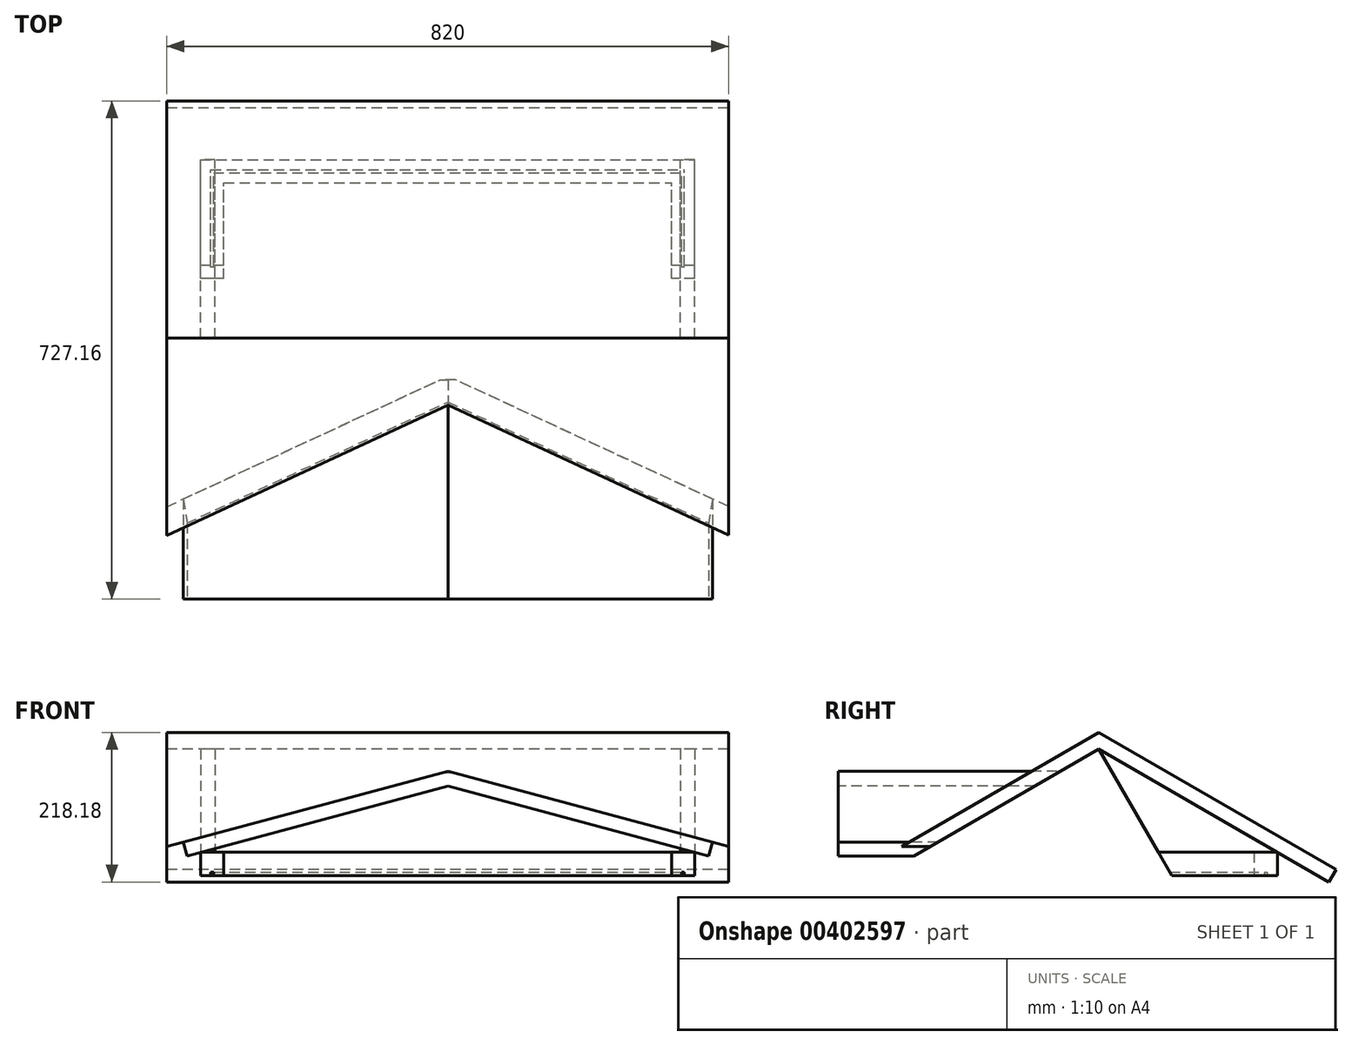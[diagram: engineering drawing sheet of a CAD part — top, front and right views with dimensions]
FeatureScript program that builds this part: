
annotation { "Feature Type Name" : "Feature", "Feature Type Description" : "" }
export const myFeature = defineFeature(function(context is Context, id is Id, definition is map)
    precondition{}
    {
        {
            var Q0;
            Q0=qCreatedBy(makeId("Top.planeOp"),FACE);
            var sketch = newSketch(context, id + "F0", { "sketchPlane" : qUnion([Q0])});
            skLineSegment(sketch, "E0.bottom", {"start": v(-361.13, -297.37) * mm, "end": v(360.37, -297.37) * mm});
            skLineSegment(sketch, "E0.top", {"start": v(-361.13, 224.13) * mm, "end": v(360.37, 224.13) * mm});
            skLineSegment(sketch, "E0.left", {"start": v(-361.13, -297.37) * mm, "end": v(-361.13, 224.13) * mm});
            skLineSegment(sketch, "E0.right", {"start": v(360.37, -297.37) * mm, "end": v(360.37, 224.13) * mm});
            skLineSegment(sketch, "E1.0", {"start": v(326.37, -263.37) * mm, "end": v(326.37, 190.13) * mm});
            skLineSegment(sketch, "E1.1", {"start": v(-327.13, -263.37) * mm, "end": v(326.37, -263.37) * mm});
            skLineSegment(sketch, "E1.2", {"start": v(-327.13, -263.37) * mm, "end": v(-327.13, 190.13) * mm});
            skLineSegment(sketch, "E1.3", {"start": v(-327.13, 190.13) * mm, "end": v(326.37, 190.13) * mm});
            skLineSegment(sketch, "E2.0", {"start": v(341.37, -278.37) * mm, "end": v(341.37, 205.13) * mm});
            skLineSegment(sketch, "E2.1", {"start": v(-342.13, -278.37) * mm, "end": v(341.37, -278.37) * mm});
            skLineSegment(sketch, "E2.2", {"start": v(-342.13, -278.37) * mm, "end": v(-342.13, 205.13) * mm});
            skLineSegment(sketch, "E2.3", {"start": v(-342.13, 205.13) * mm, "end": v(341.37, 205.13) * mm});
            skLineSegment(sketch, "E3.0", {"start": v(345.37, -282.37) * mm, "end": v(345.37, 209.13) * mm});
            skLineSegment(sketch, "E3.1", {"start": v(-346.13, -282.37) * mm, "end": v(345.37, -282.37) * mm});
            skLineSegment(sketch, "E3.2", {"start": v(-346.13, -282.37) * mm, "end": v(-346.13, 209.13) * mm});
            skLineSegment(sketch, "E3.3", {"start": v(-346.13, 209.13) * mm, "end": v(345.37, 209.13) * mm});
            skLineSegment(sketch, "E4", {"start": v(326.37, 190.13) * mm, "end": v(360.37, 224.13) * mm});
            skLineSegment(sketch, "E5", {"start": v(-327.13, 190.13) * mm, "end": v(-361.13, 224.13) * mm});
            skLineSegment(sketch, "E6", {"start": v(-327.13, -263.37) * mm, "end": v(-361.13, -297.37) * mm});
            skLineSegment(sketch, "E7", {"start": v(326.37, -263.37) * mm, "end": v(360.37, -297.37) * mm});
            skSolve(sketch);
        }
        {
            var Q0;
            {var subQ0=sQuery(id+"F0.wireOp",EDGE,"E0.right");Q0=makeQuery(id+"F0.imprint","IMPRINT",FACE,{"disambiguationData":[TD([[makeQuery(id+"F0.imprint","IMPRINT",EDGE,{"derivedFrom":subQ0}),1.0]])]});}
            var Q1;
            {var subQ0=sQuery(id+"F0.wireOp",EDGE,"E1.0");Q1=makeQuery(id+"F0.imprint","IMPRINT",FACE,{"disambiguationData":[TD([[makeQuery(id+"F0.imprint","IMPRINT",EDGE,{"derivedFrom":subQ0}),-1.0]])]});}
            var Q2;
            {var subQ0=sQuery(id+"F0.wireOp",EDGE,"E0.bottom");Q2=makeQuery(id+"F0.imprint","IMPRINT",FACE,{"disambiguationData":[TD([[makeQuery(id+"F0.imprint","IMPRINT",EDGE,{"derivedFrom":subQ0}),1.0]])]});}
            var Q3;
            {var subQ0=sQuery(id+"F0.wireOp",EDGE,"E0.top");Q3=makeQuery(id+"F0.imprint","IMPRINT",FACE,{"disambiguationData":[TD([[makeQuery(id+"F0.imprint","IMPRINT",EDGE,{"derivedFrom":subQ0}),-1.0]])]});}
            var Q4;
            {var subQ0=sQuery(id+"F0.wireOp",EDGE,"E0.left");Q4=makeQuery(id+"F0.imprint","IMPRINT",FACE,{"disambiguationData":[TD([[makeQuery(id+"F0.imprint","IMPRINT",EDGE,{"derivedFrom":subQ0}),-1.0]])]});}
            var Q5;
            {var subQ0=sQuery(id+"F0.wireOp",EDGE,"E1.1");Q5=makeQuery(id+"F0.imprint","IMPRINT",FACE,{"disambiguationData":[TD([[makeQuery(id+"F0.imprint","IMPRINT",EDGE,{"derivedFrom":subQ0}),-1.0]])]});}
            var Q6;
            {var subQ0=sQuery(id+"F0.wireOp",EDGE,"E1.2");Q6=makeQuery(id+"F0.imprint","IMPRINT",FACE,{"disambiguationData":[TD([[makeQuery(id+"F0.imprint","IMPRINT",EDGE,{"derivedFrom":subQ0}),1.0]])]});}
            var Q7;
            {var subQ0=sQuery(id+"F0.wireOp",EDGE,"E1.3");Q7=makeQuery(id+"F0.imprint","IMPRINT",FACE,{"disambiguationData":[TD([[makeQuery(id+"F0.imprint","IMPRINT",EDGE,{"derivedFrom":subQ0}),1.0]])]});}
            var Q8;
            {var subQ0=sQuery(id+"F0.wireOp",EDGE,"E2.0");Q8=makeQuery(id+"F0.imprint","IMPRINT",FACE,{"disambiguationData":[TD([[makeQuery(id+"F0.imprint","IMPRINT",EDGE,{"derivedFrom":subQ0}),-1.0]])]});}
            var Q9;
            {var subQ0=sQuery(id+"F0.wireOp",EDGE,"E2.1");Q9=makeQuery(id+"F0.imprint","IMPRINT",FACE,{"disambiguationData":[TD([[makeQuery(id+"F0.imprint","IMPRINT",EDGE,{"derivedFrom":subQ0}),-1.0]])]});}
            var Q10;
            {var subQ0=sQuery(id+"F0.wireOp",EDGE,"E2.2");Q10=makeQuery(id+"F0.imprint","IMPRINT",FACE,{"disambiguationData":[TD([[makeQuery(id+"F0.imprint","IMPRINT",EDGE,{"derivedFrom":subQ0}),1.0]])]});}
            var Q11;
            {var subQ0=sQuery(id+"F0.wireOp",EDGE,"E2.3");Q11=makeQuery(id+"F0.imprint","IMPRINT",FACE,{"disambiguationData":[TD([[makeQuery(id+"F0.imprint","IMPRINT",EDGE,{"derivedFrom":subQ0}),1.0]])]});}
            extrude(context, id + "F1", {"entities" : qUnion([Q0, Q1, Q2, Q3, Q4, Q5, Q6, Q7, Q8, Q9, Q10, Q11]), "depth" : 34 * mm});
        }
        {
            var Q0;
            Q0=makeQuery(id+"F1.opExtrude","SWEPT_FACE",FACE,{"disambiguationData":[OSD([sQuery(id+"F0.wireOp",EDGE,"E0.left")])]});
            var sketch = newSketch(context, id + "F2", { "sketchPlane" : qUnion([Q0])});
            skLineSegment(sketch, "E8", {"start": v(36.62, 34) * mm, "end": v(36.62, 184.54) * mm});
            skLineSegment(sketch, "E9", {"start": v(36.62, 184.54) * mm, "end": v(297.37, 34) * mm});
            skLineSegment(sketch, "E10", {"start": v(297.37, 34) * mm, "end": v(372.53, -9.4) * mm});
            skLineSegment(sketch, "E11", {"start": v(372.53, -9.4) * mm, "end": v(383.03, 8.8) * mm});
            skLineSegment(sketch, "E12", {"start": v(383.03, 8.8) * mm, "end": v(36.62, 208.8) * mm});
            skLineSegment(sketch, "E13", {"start": v(36.62, 208.8) * mm, "end": v(36.62, 184.54) * mm});
            skLineSegment(sketch, "E14.MirrorCS", {"start": v(-299.29, -9.4) * mm, "end": v(-309.79, 8.8) * mm});
            skLineSegment(sketch, "E15.MirrorCS", {"start": v(-224.13, 34) * mm, "end": v(-299.29, -9.4) * mm});
            skLineSegment(sketch, "E16.MirrorCS", {"start": v(-309.79, 8.8) * mm, "end": v(36.62, 208.8) * mm});
            skLineSegment(sketch, "E17.MirrorCS", {"start": v(36.62, 184.54) * mm, "end": v(-224.13, 34) * mm});
            skLineSegment(sketch, "E18", {"start": v(-224.13, 34) * mm, "end": v(-203.13, 34) * mm});
            skLineSegment(sketch, "E19.MirrorCS", {"start": v(276.37, 34) * mm, "end": v(276.37, 46.12) * mm});
            skSolve(sketch);
        }
        {
            var Q0;
            Q0=makeQuery(id+"F2.imprint","IMPRINT",FACE,{"disambiguationData":[TD([[makeQuery(id+"F2.imprint","IMPRINT",EDGE,{"derivedFrom":sQuery(id+"F2.wireOp",EDGE,"E14.MirrorCS")}),-1.0]])]});
            var Q1;
            Q1=makeQuery(id+"F2.imprint","IMPRINT",FACE,{"disambiguationData":[TD([[makeQuery(id+"F2.imprint","IMPRINT",EDGE,{"derivedFrom":sQuery(id+"F2.wireOp",EDGE,"E9")}),1.0]])]});
            extrude(context, id + "F3", {"entities" : qUnion([Q0, Q1]), "oppositeDirection" : true, "depth" : (721.5 + 49.25) * mm, "hasSecondDirection" : true, "secondDirectionOppositeDirection" : false, "secondDirectionDepth" : 49.25 * mm});
        }
        {
            var Q0;
            {var subQ0=sQuery(id+"F2.wireOp",EDGE,"E8");Q0=makeQuery(id+"F2.imprint","IMPRINT",FACE,{"disambiguationData":[TD([[makeQuery(id+"F2.imprint","IMPRINT",EDGE,{"derivedFrom":subQ0}),1.0]])]});}
            var Q1;
            {var subQ0=sQuery(id+"F2.wireOp",EDGE,"E8");Q1=makeQuery(id+"F2.imprint","IMPRINT",FACE,{"disambiguationData":[TD([[makeQuery(id+"F2.imprint","IMPRINT",EDGE,{"derivedFrom":subQ0}),-1.0]])]});}
            extrude(context, id + "F4", {"entities" : qUnion([Q0, Q1]), "oppositeDirection" : true, "depth" : 21 * mm});
        }
        {
            var Q0;
            {var subQ0=sQuery(id+"F2.wireOp",EDGE,"E8");Q0=makeQuery(id+"F2.imprint","IMPRINT",FACE,{"disambiguationData":[TD([[makeQuery(id+"F2.imprint","IMPRINT",EDGE,{"derivedFrom":subQ0}),1.0]])]});}
            var Q1;
            {var subQ0=sQuery(id+"F2.wireOp",EDGE,"E8");Q1=makeQuery(id+"F2.imprint","IMPRINT",FACE,{"disambiguationData":[TD([[makeQuery(id+"F2.imprint","IMPRINT",EDGE,{"derivedFrom":subQ0}),-1.0]])]});}
            extrude(context, id + "F5", {"entities" : qUnion([Q0, Q1]), "oppositeDirection" : true, "depth" : 721.5 * mm, "hasSecondDirection" : true, "secondDirectionOppositeDirection" : true, "secondDirectionDepth" : (721.5 - 21) * mm});
        }
        {
            var Q0;
            {var subQ0=sQuery(id+"F0.wireOp",EDGE,"E2.3");Q0=makeQuery(id+"F0.imprint","IMPRINT",FACE,{"disambiguationData":[TD([[makeQuery(id+"F0.imprint","IMPRINT",EDGE,{"derivedFrom":subQ0}),1.0]])]});}
            var Q1;
            {var subQ0=sQuery(id+"F0.wireOp",EDGE,"E2.2");Q1=makeQuery(id+"F0.imprint","IMPRINT",FACE,{"disambiguationData":[TD([[makeQuery(id+"F0.imprint","IMPRINT",EDGE,{"derivedFrom":subQ0}),1.0]])]});}
            var Q2;
            {var subQ0=sQuery(id+"F0.wireOp",EDGE,"E2.1");Q2=makeQuery(id+"F0.imprint","IMPRINT",FACE,{"disambiguationData":[TD([[makeQuery(id+"F0.imprint","IMPRINT",EDGE,{"derivedFrom":subQ0}),-1.0]])]});}
            var Q3;
            {var subQ0=sQuery(id+"F0.wireOp",EDGE,"E2.0");Q3=makeQuery(id+"F0.imprint","IMPRINT",FACE,{"disambiguationData":[TD([[makeQuery(id+"F0.imprint","IMPRINT",EDGE,{"derivedFrom":subQ0}),-1.0]])]});}
            extrude(context, id + "F6", {"entities" : qUnion([Q0, Q1, Q2, Q3]), "operationType" : NewBodyOperationType.REMOVE, "depth" : 5 * mm});
        }
        {
            var Q0;
            Q0=makeQuery(id+"F1.opExtrude","SWEPT_FACE",FACE,{"disambiguationData":[OSD([sQuery(id+"F0.wireOp",EDGE,"E0.bottom")])]});
            var sketch = newSketch(context, id + "F7", { "sketchPlane" : qUnion([Q0])});
            skLineSegment(sketch, "E20", {"start": v(-361.13, 34) * mm, "end": v(0, 130.76) * mm});
            skLineSegment(sketch, "E21", {"start": v(-361.13, 34) * mm, "end": v(-380.94, 28.7) * mm});
            skLineSegment(sketch, "E22", {"start": v(-380.94, 28.7) * mm, "end": v(-386.37, 48.98) * mm});
            skLineSegment(sketch, "E23", {"start": v(-386.37, 48.98) * mm, "end": v(0, 152.5) * mm});
            skLineSegment(sketch, "E24", {"start": v(0, 152.5) * mm, "end": v(0, 130.76) * mm});
            skLineSegment(sketch, "E25", {"start": v(0, 152.5) * mm, "end": v(0, 324.49) * mm});
            skLineSegment(sketch, "E26.MirrorCS", {"start": v(361.13, 34) * mm, "end": v(0, 130.76) * mm});
            skLineSegment(sketch, "E27.MirrorCS", {"start": v(361.13, 34) * mm, "end": v(380.94, 28.7) * mm});
            skLineSegment(sketch, "E28.MirrorCS", {"start": v(386.37, 48.98) * mm, "end": v(0, 152.5) * mm});
            skLineSegment(sketch, "E29.MirrorCS", {"start": v(380.94, 28.7) * mm, "end": v(386.37, 48.98) * mm});
            skLineSegment(sketch, "E30", {"start": v(-361.13, 34) * mm, "end": v(361.13, 34) * mm});
            skLineSegment(sketch, "E31", {"start": v(-386.37, 48.98) * mm, "end": v(-569.15, 0) * mm});
            skLineSegment(sketch, "E32", {"start": v(-569.15, 0) * mm, "end": v(569.15, 0) * mm});
            skLineSegment(sketch, "E33", {"start": v(386.37, 48.98) * mm, "end": v(569.15, 0) * mm});
            skSolve(sketch);
        }
        {
            var Q0;
            {var subQ0=sQuery(id+"F7.wireOp",EDGE,"E20");Q0=makeQuery(id+"F7.imprint","IMPRINT",FACE,{"disambiguationData":[TD([[makeQuery(id+"F7.imprint","IMPRINT",EDGE,{"derivedFrom":subQ0}),-1.0]])]});}
            extrude(context, id + "F8", {"entities" : qUnion([Q0]), "oppositeDirection" : true, "depth" : 21 * mm});
        }
        {
            var Q0;
            Q0=makeQuery(id+"F7.imprint","IMPRINT",FACE,{"disambiguationData":[TD([[makeQuery(id+"F7.imprint","IMPRINT",EDGE,{"derivedFrom":sQuery(id+"F7.wireOp",EDGE,"E21")}),1.0]])]});
            var Q1;
            Q1=makeQuery(id+"F7.imprint","IMPRINT",FACE,{"disambiguationData":[TD([[makeQuery(id+"F7.imprint","IMPRINT",EDGE,{"derivedFrom":sQuery(id+"F7.wireOp",EDGE,"E20")}),1.0]])]});
            var Q2;
            {var subQ4=sQuery(id+"F7.wireOp",EDGE,"E27.MirrorCS");Q2=makeQuery(id+"F7.imprint","IMPRINT",FACE,{"disambiguationData":[TD([[makeQuery(id+"F7.imprint","IMPRINT",EDGE,{"derivedFrom":subQ4}),-1.0]])]});}
            var Q3;
            Q3=makeQuery(id+"F7.imprint","IMPRINT",FACE,{"disambiguationData":[TD([[makeQuery(id+"F7.imprint","IMPRINT",EDGE,{"derivedFrom":sQuery(id+"F7.wireOp",EDGE,"E24")}),1.0]])]});
            var Q4;
            {var subQ0=sQuery(id+"F7.wireOp",EDGE,"E20");Q4=makeQuery(id+"F7.imprint","IMPRINT",FACE,{"disambiguationData":[TD([[makeQuery(id+"F7.imprint","IMPRINT",EDGE,{"derivedFrom":subQ0}),-1.0]])]});}
            var Q5;
            {var subQ1=sQuery(id+"F0.wireOp",EDGE,"E0.bottom");var subQ2=makeQuery(id+"F1.opExtrude","SWEPT_EDGE",EDGE,{"disambiguationData":[OSD([subQ1,sQuery(id+"F0.wireOp",EDGE,"E0.left"),sQuery(id+"F0.wireOp",EDGE,"E6")])]});Q5=makeQuery(id+"F7.imprint","IMPRINT",FACE,{"disambiguationData":[TD([[makeQuery(id+"F7.imprint","IMPRINT",EDGE,{"derivedFrom":subQ2}),1.0]])]});}
            extrude(context, id + "F9", {"entities" : qUnion([Q0, Q1, Q2, Q3, Q4, Q5]), "operationType" : NewBodyOperationType.REMOVE, "oppositeDirection" : true, "depth" : 200 * mm, "hasSecondDirection" : true, "secondDirectionOppositeDirection" : false, "secondDirectionDepth" : 50 * mm});
        }
        {
            var Q0;
            Q0=makeQuery(id+"F3.opExtrude","SWEPT_FACE",FACE,{"disambiguationData":[OSD([sQuery(id+"F2.wireOp",EDGE,"E12")])]});
            var sketch = newSketch(context, id + "F10", { "sketchPlane" : qUnion([Q0])});
            skLineSegment(sketch, "E34", {"start": v(0, -39.9) * mm, "end": v(-612.66, -368.22) * mm});
            skLineSegment(sketch, "E35", {"start": v(0, -39.9) * mm, "end": v(612.66, -368.22) * mm});
            skLineSegment(sketch, "E36", {"start": v(612.66, -368.22) * mm, "end": v(-612.66, -368.22) * mm});
            skSolve(sketch);
        }
        {
            var Q0;
            {var subQ0=sQuery(id+"F2.wireOp",EDGE,"E12");var subQ1=makeQuery(id+"F3.opExtrude","SWEPT_EDGE",EDGE,{"disambiguationData":[OSD([sQuery(id+"F2.wireOp",EDGE,"E11"),subQ0])]});Q0=makeQuery(id+"F10.imprint","IMPRINT",FACE,{"disambiguationData":[TD([[makeQuery(id+"F10.imprint","IMPRINT",EDGE,{"derivedFrom":subQ1}),-1.0]])]});}
            extrude(context, id + "F11", {"entities" : qUnion([Q0]), "operationType" : NewBodyOperationType.REMOVE, "oppositeDirection" : true, "depth" : 50 * mm, "hasDraft" : true, "draftAngle" : 3 * degree});
        }
        {
            var Q0;
            Q0=makeQuery(id+"F7.imprint","IMPRINT",FACE,{"disambiguationData":[TD([[makeQuery(id+"F7.imprint","IMPRINT",EDGE,{"derivedFrom":sQuery(id+"F7.wireOp",EDGE,"E24")}),1.0]])]});
            var Q1;
            Q1=makeQuery(id+"F7.imprint","IMPRINT",FACE,{"disambiguationData":[TD([[makeQuery(id+"F7.imprint","IMPRINT",EDGE,{"derivedFrom":sQuery(id+"F7.wireOp",EDGE,"E20")}),1.0]])]});
            extrude(context, id + "F12", {"entities" : qUnion([Q0, Q1]), "oppositeDirection" : true, "depth" : 200 * mm, "hasSecondDirection" : true, "secondDirectionOppositeDirection" : false, "secondDirectionDepth" : 120 * mm});
        }
        {
            var Q0;
            {var subQ4=sQuery(id+"F2.wireOp",EDGE,"E17.MirrorCS");var subQ6=sQuery(id+"F2.wireOp",EDGE,"E15.MirrorCS");var subQ10=sQuery(id+"F2.wireOp",EDGE,"E10");var subQ11=sQuery(id+"F2.wireOp",EDGE,"E9");Q0=makeQuery(id+"F9.boolean.opBoolean","SPLIT",FACE,{"disambiguationData":[TD([makeQuery(id+"F3.opExtrude","SWEPT_FACE",FACE,{"disambiguationData":[OSD([subQ6,subQ4])]})])],"derivedFrom":makeQuery(id+"F3.opExtrude","SWEPT_FACE",FACE,{"disambiguationData":[OSD([subQ11,subQ10])]})});}
            var sketch = newSketch(context, id + "F13", { "sketchPlane" : qUnion([Q0])});
            skLineSegment(sketch, "E37.bottom", {"start": v(409.62, -60.55) * mm, "end": v(-410.38, -60.55) * mm});
            skLineSegment(sketch, "E37.top", {"start": v(409.62, 223.44) * mm, "end": v(-410.38, 223.44) * mm});
            skLineSegment(sketch, "E37.left", {"start": v(409.62, -60.55) * mm, "end": v(409.62, 223.44) * mm});
            skLineSegment(sketch, "E37.right", {"start": v(-410.38, -60.55) * mm, "end": v(-410.38, 223.44) * mm});
            skSolve(sketch);
        }
        {
            var Q0;
            {var subQ1=sQuery(id+"F13.wireOp",EDGE,"E37.bottom");Q0=makeQuery(id+"F13.imprint","IMPRINT",FACE,{"disambiguationData":[TD([[makeQuery(id+"F13.imprint","IMPRINT",EDGE,{"derivedFrom":subQ1}),-1.0]])]});}
            extrude(context, id + "F14", {"entities" : qUnion([Q0]), "operationType" : NewBodyOperationType.REMOVE, "depth" : 300 * mm});
        }
        {
            var Q0;
            {var subQ0=sQuery(id+"F2.wireOp",EDGE,"E17.MirrorCS");var subQ1=sQuery(id+"F2.wireOp",EDGE,"E15.MirrorCS");var subQ2=sQuery(id+"F2.wireOp",EDGE,"E12");var subQ3=sQuery(id+"F2.wireOp",EDGE,"E14.MirrorCS");var subQ4=sQuery(id+"F2.wireOp",EDGE,"E10");var subQ5=sQuery(id+"F2.wireOp",EDGE,"E9");var subQ6=sQuery(id+"F2.wireOp",EDGE,"E16.MirrorCS");Q0=makeQuery(id+"F9.boolean.opBoolean","SPLIT",FACE,{"disambiguationData":[TD([makeQuery(id+"F3.opExtrude","SWEPT_FACE",FACE,{"disambiguationData":[OSD([subQ3])]})])],"derivedFrom":makeQuery(id+"F3.opExtrude","CAP_FACE",FACE,{"disambiguationData":[OSD([subQ5,subQ4,sQuery(id+"F2.wireOp",EDGE,"E11"),subQ2,subQ3,subQ1,subQ6,subQ0])],"isStart":false})});}
            var sketch = newSketch(context, id + "F15", { "sketchPlane" : qUnion([Q0])});
            skLineSegment(sketch, "E38", {"start": v(-36.62, 184.54) * mm, "end": v(-52.36, 175.46) * mm});
            skLineSegment(sketch, "E39", {"start": v(-52.36, 175.46) * mm, "end": v(-24.59, 127.35) * mm});
            skLineSegment(sketch, "E40", {"start": v(-24.59, 127.35) * mm, "end": v(-403.72, -91.54) * mm});
            skLineSegment(sketch, "E41", {"start": v(-282.23, 42.75) * mm, "end": v(-409.62, -30.8) * mm});
            skLineSegment(sketch, "E42", {"start": v(-409.62, -30.8) * mm, "end": v(-403.72, -91.54) * mm});
            skLineSegment(sketch, "E43", {"start": v(-282.23, 42.75) * mm, "end": v(-52.36, 175.46) * mm});
            skSolve(sketch);
        }
        {
            var Q0;
            Q0=makeQuery(id+"F15.imprint","IMPRINT",FACE,{"disambiguationData":[TD([[makeQuery(id+"F15.imprint","IMPRINT",EDGE,{"derivedFrom":sQuery(id+"F15.wireOp",EDGE,"E39")}),-1.0]])]});
            extrude(context, id + "F16", {"entities" : qUnion([Q0]), "operationType" : NewBodyOperationType.REMOVE, "oppositeDirection" : true, "depth" : 800 * mm});
        }
    });
